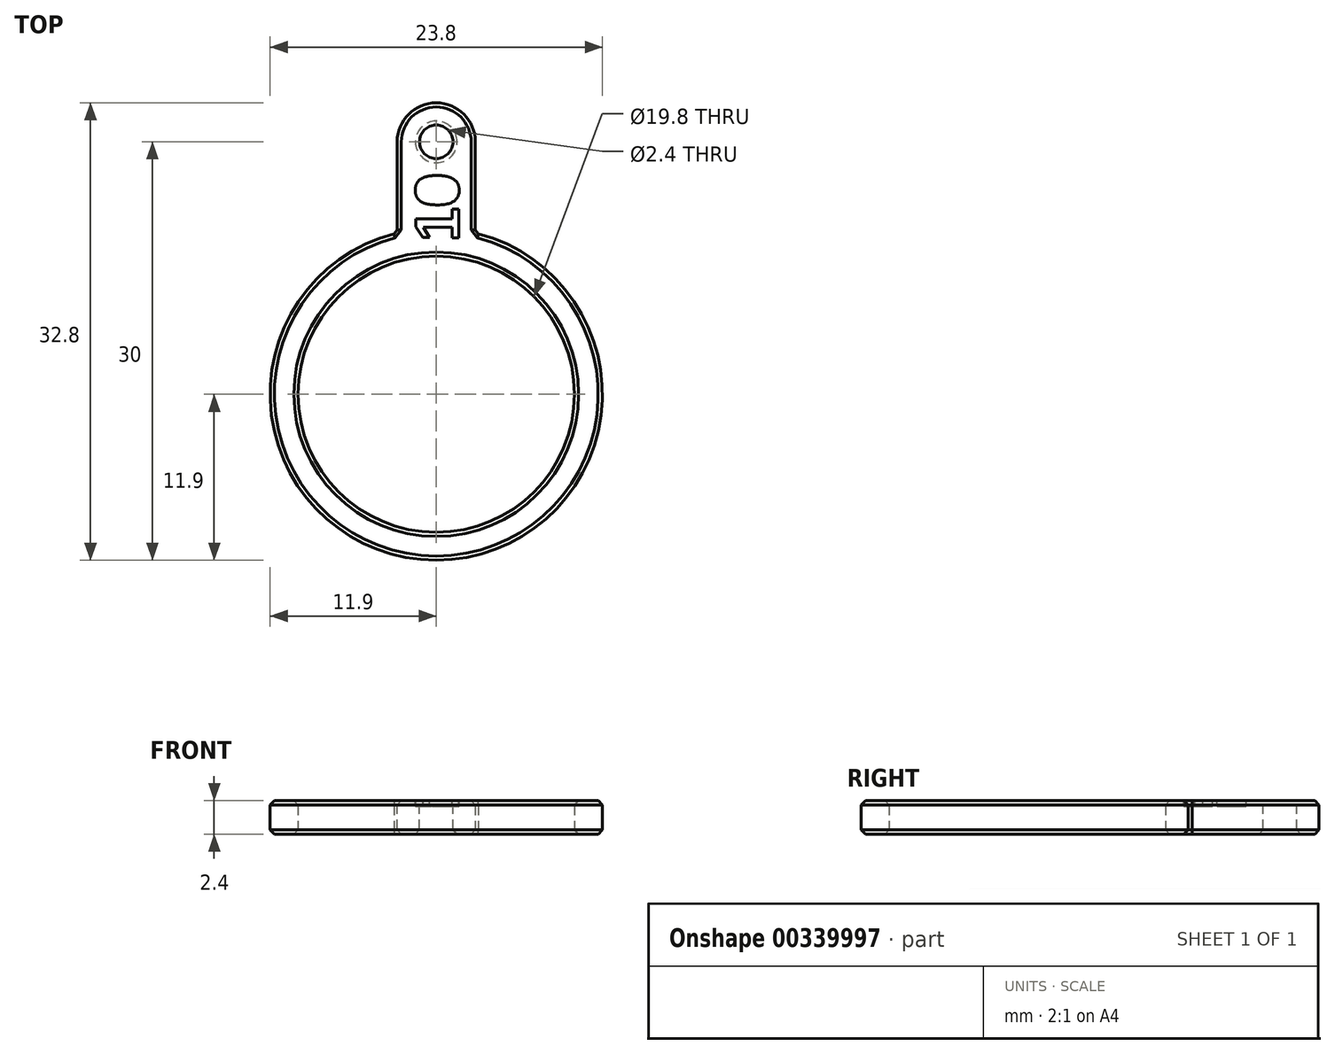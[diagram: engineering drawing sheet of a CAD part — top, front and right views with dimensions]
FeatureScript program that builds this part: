
annotation { "Feature Type Name" : "Feature", "Feature Type Description" : "" }
export const myFeature = defineFeature(function(context is Context, id is Id, definition is map)
    precondition{}
    {
        {
            var Q0;
            Q0=qCreatedBy(makeId("Top.planeOp"),FACE);
            var sketch = newSketch(context, id + "F0", { "sketchPlane" : qUnion([Q0])});
            skCircle(sketch, "E0", {"center": v(0, 0) * mm, "radius": 9.9 * mm});
            skCircle(sketch, "E1", {"center": v(0, 0) * mm, "radius": 11.9 * mm});
            skLineSegment(sketch, "E2.bottom", {"start": v(2.8, 2.9) * mm, "end": v(-2.8, 2.9) * mm});
            skLineSegment(sketch, "E2.top", {"start": v(2.8, 20.9) * mm, "end": v(-2.8, 20.9) * mm});
            skLineSegment(sketch, "E2.left", {"start": v(2.8, 2.9) * mm, "end": v(2.8, 20.9) * mm});
            skLineSegment(sketch, "E2.right", {"start": v(-2.8, 2.9) * mm, "end": v(-2.8, 20.9) * mm});
            skPoint(sketch, "E2.middle", {"position": v(0, 11.9) * mm});
            skSolve(sketch);
        }
        {
            var Q0;
            Q0=qSketchRegion(id+"F0",true);
            extrude(context, id + "F1", {"entities" : qUnion([Q0]), "depth" : 2.4 * mm});
        }
        {
            var Q0;
            Q0=makeQuery(id+"F1.opExtrude","SWEPT_EDGE",EDGE,{"disambiguationData":[OSD([sQuery(id+"F0.wireOp",EDGE,"E2.top"),sQuery(id+"F0.wireOp",EDGE,"E2.right")])]});
            var Q1;
            Q1=makeQuery(id+"F1.opExtrude","SWEPT_EDGE",EDGE,{"disambiguationData":[OSD([sQuery(id+"F0.wireOp",EDGE,"E2.top"),sQuery(id+"F0.wireOp",EDGE,"E2.left")])]});
            fillet(context, id + "F2", {"entities" : qUnion([Q0, Q1]), "radius" : 2.8 * mm, "tangentPropagation" : true, "allowEdgeOverflow" : false});
        }
        {
            var Q0;
            Q0=makeQuery(id+"F1.opExtrude","CAP_FACE",FACE,{"disambiguationData":[OSD([sQuery(id+"F0.wireOp",EDGE,"E0"),sQuery(id+"F0.wireOp",EDGE,"E1"),sQuery(id+"F0.wireOp",EDGE,"E2.top"),sQuery(id+"F0.wireOp",EDGE,"E2.left"),sQuery(id+"F0.wireOp",EDGE,"E2.right")])],"isStart":false});
            var sketch = newSketch(context, id + "F3", { "sketchPlane" : qUnion([Q0])});
            skCircle(sketch, "E3", {"center": v(0, 18.1) * mm, "radius": 1.2 * mm});
            skSolve(sketch);
        }
        {
            var Q0;
            Q0=qSketchRegion(id+"F3",true);
            extrude(context, id + "F4", {"entities" : qUnion([Q0]), "operationType" : NewBodyOperationType.REMOVE, "oppositeDirection" : true, "depth" : 25 * mm});
        }
        {
            var Q0;
            Q0=makeQuery(id+"F4.boolean.opBoolean","COPY",EDGE,{"derivedFrom":makeQuery(id+"F4.opExtrude","CAP_EDGE",EDGE,{"disambiguationData":[OSD([sQuery(id+"F3.wireOp",EDGE,"E3")])],"isStart":true})});
            var Q1;
            Q1=makeQuery(id+"F4.boolean.opBoolean","INTERSECT",EDGE,{"derivedFrom":[makeQuery(id+"F1.opExtrude","CAP_FACE",FACE,{"disambiguationData":[OSD([sQuery(id+"F0.wireOp",EDGE,"E0"),sQuery(id+"F0.wireOp",EDGE,"E1"),sQuery(id+"F0.wireOp",EDGE,"E2.top"),sQuery(id+"F0.wireOp",EDGE,"E2.left"),sQuery(id+"F0.wireOp",EDGE,"E2.right")])],"isStart":true}),makeQuery(id+"F4.opExtrude","SWEPT_FACE",FACE,{"disambiguationData":[OSD([sQuery(id+"F3.wireOp",EDGE,"E3")])]})]});
            var Q2;
            {var subQ0=sQuery(id+"F0.wireOp",EDGE,"E2.right");var subQ1=sQuery(id+"F0.wireOp",EDGE,"E2.top");Q2=makeQuery(id+"F2.opFillet","BLEND_EDGE",EDGE,{"blendedFrom":[makeQuery(id+"F1.opExtrude","SWEPT_EDGE",EDGE,{"disambiguationData":[OSD([subQ1,subQ0])]}),makeQuery(id+"F1.opExtrude","CAP_FACE",FACE,{"disambiguationData":[OSD([sQuery(id+"F0.wireOp",EDGE,"E0"),sQuery(id+"F0.wireOp",EDGE,"E1"),subQ1,sQuery(id+"F0.wireOp",EDGE,"E2.left"),subQ0])],"isStart":true})],"blendedInto":[makeQuery(id+"F1.opExtrude","CAP_FACE",FACE,{"disambiguationData":[OSD([sQuery(id+"F0.wireOp",EDGE,"E0"),sQuery(id+"F0.wireOp",EDGE,"E1"),subQ1,sQuery(id+"F0.wireOp",EDGE,"E2.left"),subQ0])],"isStart":true})]});}
            var Q3;
            {var subQ0=sQuery(id+"F0.wireOp",EDGE,"E2.right");var subQ1=sQuery(id+"F0.wireOp",EDGE,"E2.top");Q3=makeQuery(id+"F2.opFillet","BLEND_EDGE",EDGE,{"blendedFrom":[makeQuery(id+"F1.opExtrude","SWEPT_EDGE",EDGE,{"disambiguationData":[OSD([subQ1,subQ0])]}),makeQuery(id+"F1.opExtrude","CAP_FACE",FACE,{"disambiguationData":[OSD([sQuery(id+"F0.wireOp",EDGE,"E0"),sQuery(id+"F0.wireOp",EDGE,"E1"),subQ1,sQuery(id+"F0.wireOp",EDGE,"E2.left"),subQ0])],"isStart":false})],"blendedInto":[makeQuery(id+"F1.opExtrude","CAP_FACE",FACE,{"disambiguationData":[OSD([sQuery(id+"F0.wireOp",EDGE,"E0"),sQuery(id+"F0.wireOp",EDGE,"E1"),subQ1,sQuery(id+"F0.wireOp",EDGE,"E2.left"),subQ0])],"isStart":false})]});}
            var Q4;
            Q4=makeQuery(id+"F1.opExtrude","CAP_EDGE",EDGE,{"disambiguationData":[OSD([sQuery(id+"F0.wireOp",EDGE,"E1")])],"isStart":false});
            var Q5;
            Q5=makeQuery(id+"F1.opExtrude","CAP_EDGE",EDGE,{"disambiguationData":[OSD([sQuery(id+"F0.wireOp",EDGE,"E1")])],"isStart":true});
            var Q6;
            Q6=makeQuery(id+"F1.opExtrude","SWEPT_EDGE",EDGE,{"disambiguationData":[OSD([sQuery(id+"F0.wireOp",EDGE,"E1"),sQuery(id+"F0.wireOp",EDGE,"E2.left")])]});
            var Q7;
            Q7=makeQuery(id+"F1.opExtrude","SWEPT_EDGE",EDGE,{"disambiguationData":[OSD([sQuery(id+"F0.wireOp",EDGE,"E1"),sQuery(id+"F0.wireOp",EDGE,"E2.right")])]});
            var Q8;
            Q8=makeQuery(id+"F1.opExtrude","CAP_EDGE",EDGE,{"disambiguationData":[OSD([sQuery(id+"F0.wireOp",EDGE,"E0")])],"isStart":true});
            var Q9;
            Q9=makeQuery(id+"F1.opExtrude","CAP_EDGE",EDGE,{"disambiguationData":[OSD([sQuery(id+"F0.wireOp",EDGE,"E0")])],"isStart":false});
            chamfer(context, id + "F5", {"entities" : qUnion([Q0, Q1, Q2, Q3, Q4, Q5, Q6, Q7, Q8, Q9]), "width" : 0.3 * mm, "tangentPropagation" : true});
        }
        {
            var Q0;
            Q0=makeQuery(id+"F1.opExtrude","CAP_FACE",FACE,{"disambiguationData":[OSD([sQuery(id+"F0.wireOp",EDGE,"E0"),sQuery(id+"F0.wireOp",EDGE,"E1"),sQuery(id+"F0.wireOp",EDGE,"E2.top"),sQuery(id+"F0.wireOp",EDGE,"E2.left"),sQuery(id+"F0.wireOp",EDGE,"E2.right")])],"isStart":false});
            var sketch = newSketch(context, id + "F6", { "sketchPlane" : qUnion([Q0])});
            skText(sketch, "E4", { "text": "10", "fontName": "Arimo-Bold.ttf"});
            skLineSegment(sketch, "E5", {"start": v(0, 10.93) * mm, "end": v(0, 0) * mm});
            skPoint(sketch, "E5.endSnap0", {"position": v(0, 10.93) * mm});
            const initialGuessF6  = {"E4": [0.0016, 0.01093, 0, 1, 0.0032]};
            skSetInitialGuess(sketch, initialGuessF6);
            skSolve(sketch);
        }
        {
            var Q0;
            Q0 = qSketchRegion(id + "F6", true);
            var Q1;
            Q1=makeQuery(id+"F6.imprint","IMPRINT",FACE,{"disambiguationData":[TD([[makeQuery(id+"F6.imprint","IMPRINT",EDGE,{"derivedFrom":sQuery(id+"F6.wireOp",EDGE,"E4.sketch_text.stroke-19")}),1.0]])]});
            extrude(context, id + "F7", {"entities" : qUnion([Q0, Q1]), "operationType" : NewBodyOperationType.REMOVE, "oppositeDirection" : true, "depth" : 0.4 * mm});
        }
    });
